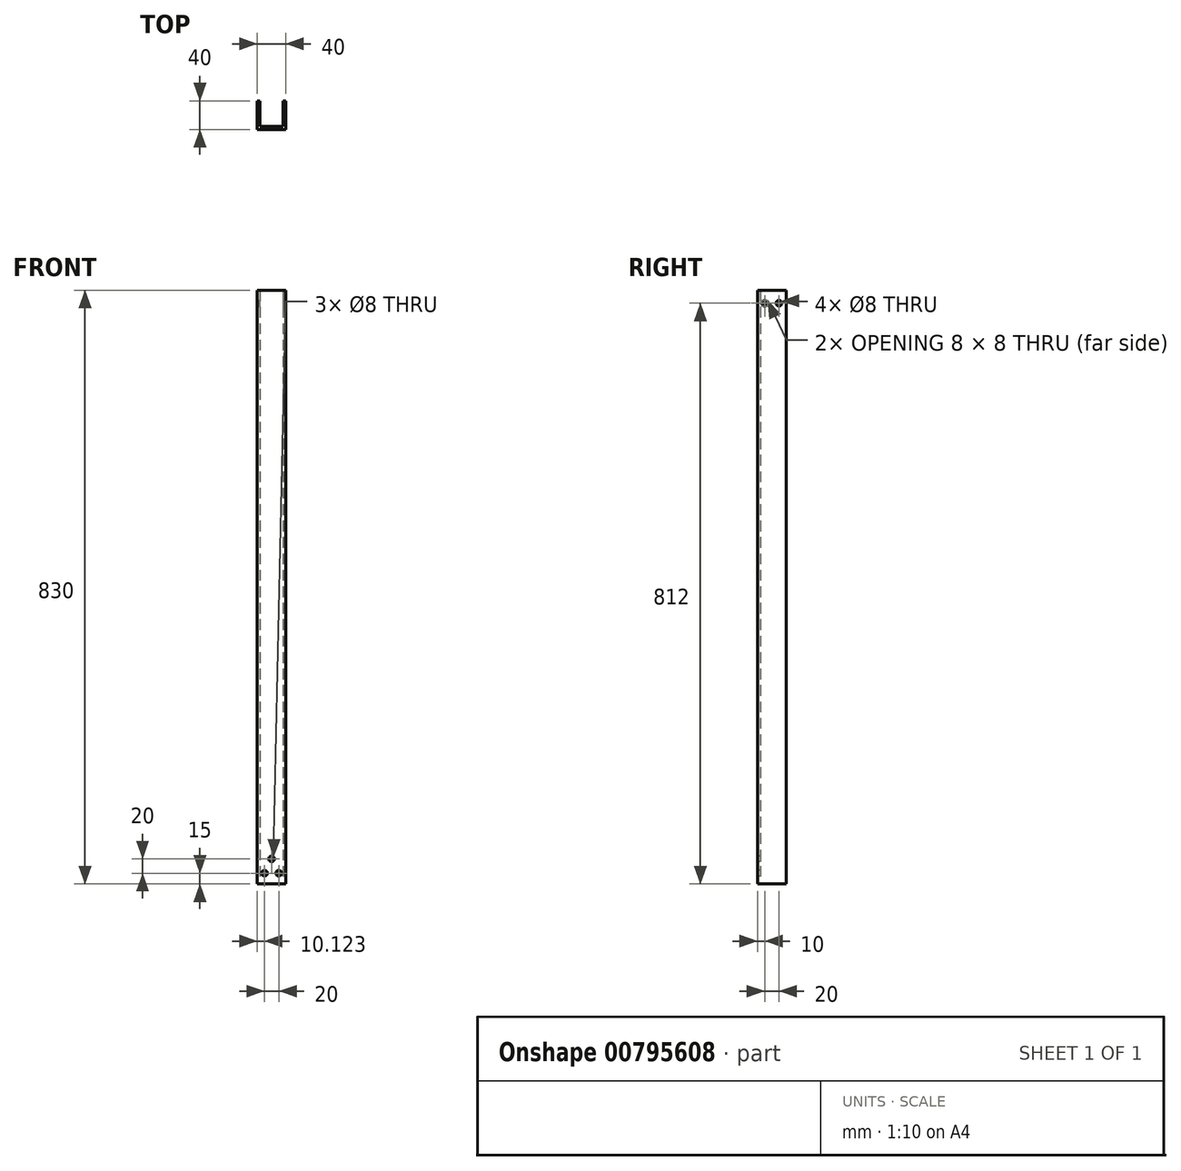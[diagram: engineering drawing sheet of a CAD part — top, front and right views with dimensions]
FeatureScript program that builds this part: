
annotation { "Feature Type Name" : "Feature", "Feature Type Description" : "" }
export const myFeature = defineFeature(function(context is Context, id is Id, definition is map)
    precondition{}
    {
        {
            var Q0;
            Q0=qCreatedBy(makeId("Top.planeOp"),FACE);
            var sketch = newSketch(context, id + "F0", { "sketchPlane" : qUnion([Q0])});
            skLineSegment(sketch, "E0.bottom", {"start": v(20, -20) * mm, "end": v(-20, -20) * mm});
            skLineSegment(sketch, "E0.top", {"start": v(20, 20) * mm, "end": v(16, 20) * mm});
            skLineSegment(sketch, "E0.left", {"start": v(20, -20) * mm, "end": v(20, 20) * mm});
            skLineSegment(sketch, "E0.right", {"start": v(-20, -20) * mm, "end": v(-20, 20) * mm});
            skPoint(sketch, "E0.middle", {"position": v(0, 0) * mm});
            skLineSegment(sketch, "E1", {"start": v(-16, 20) * mm, "end": v(-16, -16) * mm});
            skLineSegment(sketch, "E2", {"start": v(-16, -16) * mm, "end": v(16, -16) * mm});
            skLineSegment(sketch, "E3", {"start": v(16, -16) * mm, "end": v(16, 20) * mm});
            skLineSegment(sketch, "E4.trimOffspring", {"start": v(-16, 20) * mm, "end": v(-20, 20) * mm});
            skSolve(sketch);
        }
        {
            var Q0;
            Q0=makeQuery(id+"F0.imprint","IMPRINT",FACE,{"disambiguationData":[TD([[makeQuery(id+"F0.imprint","IMPRINT",EDGE,{"derivedFrom":sQuery(id+"F0.wireOp",EDGE,"E0.bottom")}),-1.0]])]});
            extrude(context, id + "F1", {"entities" : qUnion([Q0]), "endBound" : BoundingType.SYMMETRIC, "depth" : 830 * mm, "offsetDistance" : 25 * mm});
        }
        {
            var Q0;
            Q0=makeQuery(id+"F1.opExtrude","SWEPT_FACE",FACE,{"disambiguationData":[OSD([sQuery(id+"F0.wireOp",EDGE,"E0.left")])]});
            var sketch = newSketch(context, id + "F2", { "sketchPlane" : qUnion([Q0])});
            skLineSegment(sketch, "E5", {"start": v(-20, 379) * mm, "end": v(20, 379) * mm, "construction": true});
            skLineSegment(sketch, "E6", {"start": v(-20, 397) * mm, "end": v(20, 397) * mm, "construction": true});
            skCircle(sketch, "E7", {"center": v(-10, 397) * mm, "radius": 4 * mm});
            skCircle(sketch, "E8", {"center": v(10, 397) * mm, "radius": 4 * mm});
            skSolve(sketch);
        }
        {
            var Q0;
            Q0=sQuery(id+"F2.wireOp",VERTEX,"E7.center");
            var Q1;
            Q1=sQuery(id+"F2.wireOp",VERTEX,"E8.center");
            var Q2;
            Q2=makeQuery(id+"F1.opExtrude","SWEPT_BODY",BODY,{"disambiguationData":[OSD([sQuery(id+"F0.wireOp",EDGE,"E0.bottom"),sQuery(id+"F0.wireOp",EDGE,"E0.top"),sQuery(id+"F0.wireOp",EDGE,"E0.left"),sQuery(id+"F0.wireOp",EDGE,"E0.right"),sQuery(id+"F0.wireOp",EDGE,"E1"),sQuery(id+"F0.wireOp",EDGE,"E2"),sQuery(id+"F0.wireOp",EDGE,"E3"),sQuery(id+"F0.wireOp",EDGE,"E4.trimOffspring")])]});
            hole(context, id + "F3", {"style" : HoleStyle.SIMPLE, "endStyle" : HoleEndStyle.THROUGH, "standardTappedOrClearance" : lookupTablePath({ "standard" : "ISO", "size" : "8", "type" : "Drilled" }), "standardBlindInLast" : lookupTablePath({ "standard" : "ISO", "size" : "8", "type" : "Drilled" }), "holeDiameter" : 8 * mm, "majorDiameter" : 5 * mm, "isTappedThrough" : true, "tappedDepth" : 12.7 * mm, "tapClearance" : 3, "locations" : qUnion([Q0, Q1]), "scope" : qUnion([Q2])});
        }
        {
            var Q0;
            Q0=makeQuery(id+"F1.opExtrude","SWEPT_FACE",FACE,{"disambiguationData":[OSD([sQuery(id+"F0.wireOp",EDGE,"E0.bottom")])]});
            var sketch = newSketch(context, id + "F4", { "sketchPlane" : qUnion([Q0])});
            skCircle(sketch, "E9", {"center": v(-9.88, -400) * mm, "radius": 4 * mm});
            skCircle(sketch, "E10.MirrorC", {"center": v(10.12, -400) * mm, "radius": 4 * mm});
            skCircle(sketch, "E11", {"center": v(0, -380) * mm, "radius": 4 * mm});
            skLineSegment(sketch, "E12", {"start": v(-20, -370) * mm, "end": v(20, -370) * mm, "construction": true});
            skSolve(sketch);
        }
        {
            var Q0;
            Q0=sQuery(id+"F4.wireOp",VERTEX,"E11.center");
            var Q1;
            Q1=sQuery(id+"F4.wireOp",VERTEX,"E10.MirrorC.center");
            var Q2;
            Q2=sQuery(id+"F4.wireOp",VERTEX,"E9.center");
            var Q3;
            Q3=makeQuery(id+"F1.opExtrude","SWEPT_BODY",BODY,{"disambiguationData":[OSD([sQuery(id+"F0.wireOp",EDGE,"E0.bottom"),sQuery(id+"F0.wireOp",EDGE,"E0.top"),sQuery(id+"F0.wireOp",EDGE,"E0.left"),sQuery(id+"F0.wireOp",EDGE,"E0.right"),sQuery(id+"F0.wireOp",EDGE,"E1"),sQuery(id+"F0.wireOp",EDGE,"E2"),sQuery(id+"F0.wireOp",EDGE,"E3"),sQuery(id+"F0.wireOp",EDGE,"E4.trimOffspring")])]});
            hole(context, id + "F5", {"style" : HoleStyle.SIMPLE, "endStyle" : HoleEndStyle.THROUGH, "standardTappedOrClearance" : lookupTablePath({ "standard" : "ISO", "size" : "8", "type" : "Drilled" }), "standardBlindInLast" : lookupTablePath({ "standard" : "ISO", "size" : "8", "type" : "Drilled" }), "holeDiameter" : 8 * mm, "majorDiameter" : 5 * mm, "isTappedThrough" : true, "tappedDepth" : 12.7 * mm, "tapClearance" : 3, "locations" : qUnion([Q0, Q1, Q2]), "scope" : qUnion([Q3])});
        }
    });
